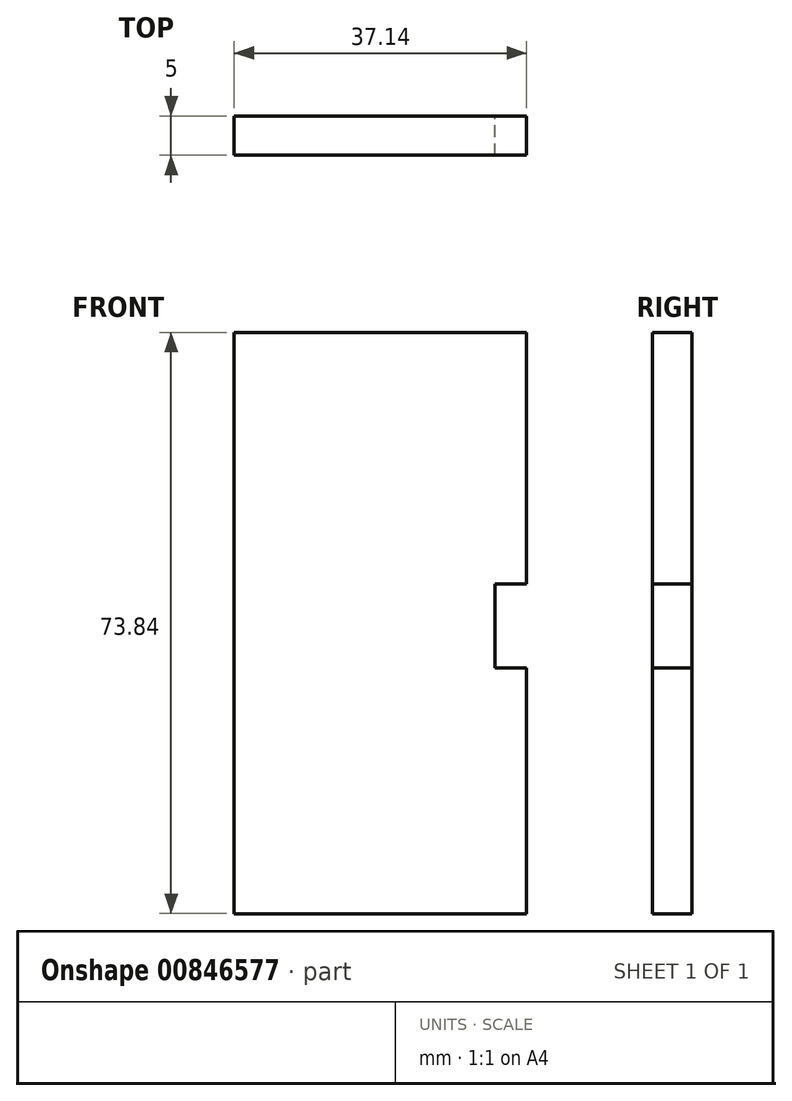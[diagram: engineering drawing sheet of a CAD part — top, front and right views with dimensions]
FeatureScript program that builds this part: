
annotation { "Feature Type Name" : "Feature", "Feature Type Description" : "" }
export const myFeature = defineFeature(function(context is Context, id is Id, definition is map)
    precondition{}
    {
        {
            var Q0;
            Q0=qCreatedBy(makeId("Front.planeOp"),FACE);
            var sketch = newSketch(context, id + "F0", { "sketchPlane" : qUnion([Q0])});
            skLineSegment(sketch, "E0.bottom", {"start": v(-18.57, 31.96) * mm, "end": v(18.57, 31.96) * mm});
            skLineSegment(sketch, "E0.top", {"start": v(-18.57, -41.88) * mm, "end": v(18.57, -41.88) * mm});
            skLineSegment(sketch, "E0.left", {"start": v(-18.57, 31.96) * mm, "end": v(-18.57, -41.88) * mm});
            skLineSegment(sketch, "E0.right", {"start": v(18.57, 31.96) * mm, "end": v(18.57, -41.88) * mm});
            skPoint(sketch, "E0.middle", {"position": v(0, -4.96) * mm});
            skLineSegment(sketch, "E1", {"start": v(18.57, 0) * mm, "end": v(14.58, 0) * mm});
            skLineSegment(sketch, "E2", {"start": v(14.58, 0) * mm, "end": v(14.58, -10.67) * mm});
            skLineSegment(sketch, "E3", {"start": v(14.58, -10.67) * mm, "end": v(18.57, -10.67) * mm});
            skLineSegment(sketch, "E4", {"start": v(18.57, -10.67) * mm, "end": v(18.57, 0) * mm});
            skSolve(sketch);
        }
        {
            var Q0;
            {var subQ1=sQuery(id+"F0.wireOp",EDGE,"E0.bottom");Q0=makeQuery(id+"F0.imprint","IMPRINT",FACE,{"disambiguationData":[TD([[makeQuery(id+"F0.imprint","IMPRINT",EDGE,{"derivedFrom":subQ1}),-1.0]])]});}
            extrude(context, id + "F1", {"entities" : qUnion([Q0]), "depth" : 5 * mm, "offsetDistance" : 25 * mm});
        }
    });
